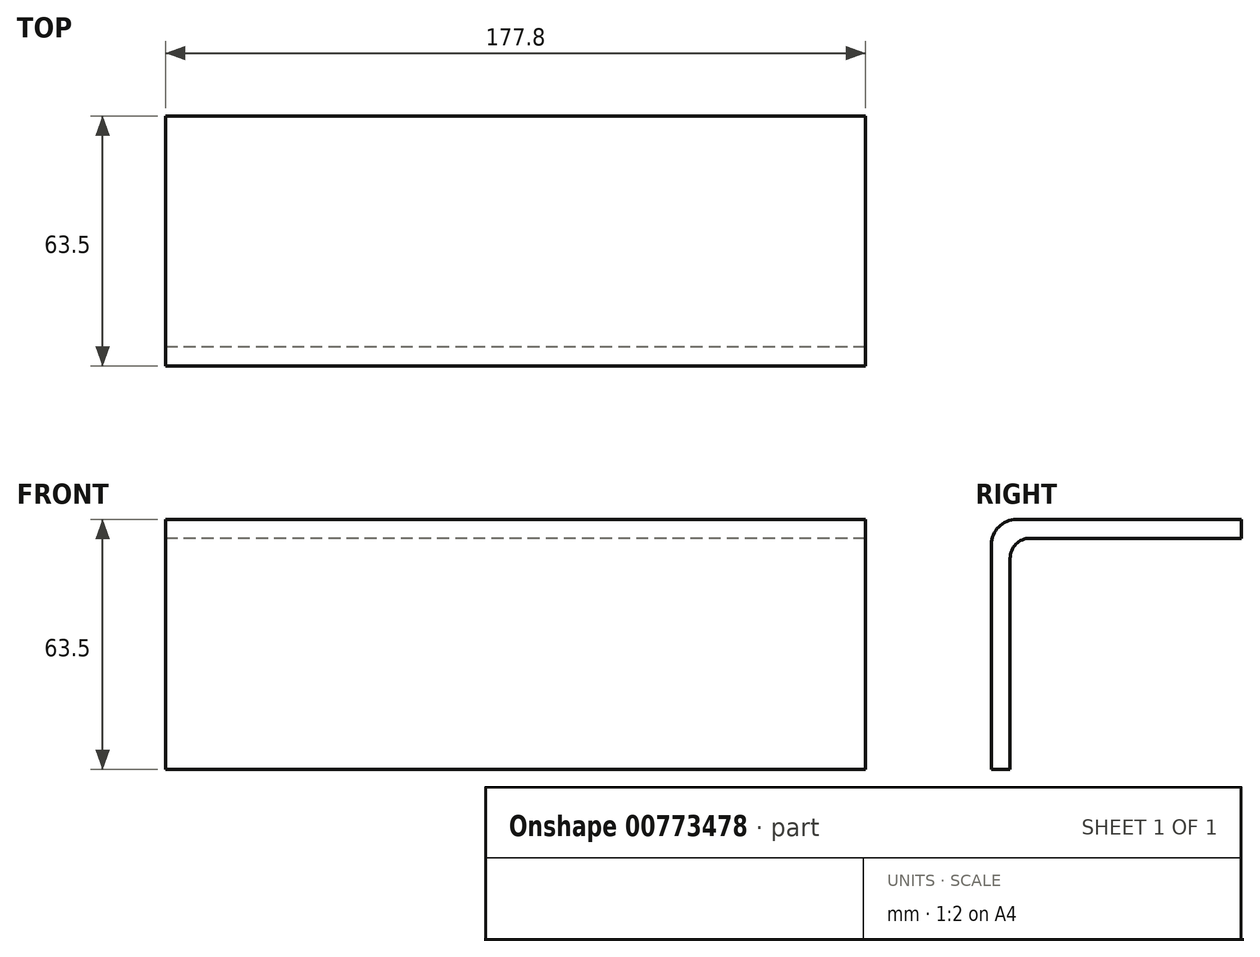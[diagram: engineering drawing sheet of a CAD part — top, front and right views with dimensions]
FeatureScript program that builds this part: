
annotation { "Feature Type Name" : "Feature", "Feature Type Description" : "" }
export const myFeature = defineFeature(function(context is Context, id is Id, definition is map)
    precondition{}
    {
        {
            var Q0;
            Q0=qCreatedBy(makeId("Right.planeOp"),FACE);
            var sketch = newSketch(context, id + "F0", { "sketchPlane" : qUnion([Q0])});
            skLineSegment(sketch, "E0", {"start": v(-28.12, -12.25) * mm, "end": v(-28.12, 44.9) * mm});
            skLineSegment(sketch, "E1", {"start": v(-21.77, 51.25) * mm, "end": v(35.38, 51.25) * mm});
            skPoint(sketch, "E2.visualSharp", {"position": v(-28.12, 51.25) * mm});
            skArc(sketch, "E2.filletArc", {"start": v(-21.77, 51.25) * mm, "mid": v(-26.26, 49.39) * mm, "end": v(-28.12, 44.9) * mm});
            skLineSegment(sketch, "E3", {"start": v(-28.12, -12.25) * mm, "end": v(-23.35, -12.25) * mm});
            skLineSegment(sketch, "E4", {"start": v(35.38, 51.25) * mm, "end": v(35.38, 46.48) * mm});
            skLineSegment(sketch, "E5", {"start": v(-23.35, -12.25) * mm, "end": v(-23.35, 41.4) * mm});
            skLineSegment(sketch, "E6", {"start": v(35.38, 46.48) * mm, "end": v(-18.27, 46.48) * mm});
            skPoint(sketch, "E7.newPointA", {"position": v(-23.35, 46.42) * mm});
            skPoint(sketch, "E7.newPointB", {"position": v(-23.29, 46.48) * mm});
            skArc(sketch, "E7.filletArc", {"start": v(-18.27, 46.48) * mm, "mid": v(-21.87, 45) * mm, "end": v(-23.35, 41.4) * mm});
            skSolve(sketch);
        }
        {
            var Q0;
            Q0=qSketchRegion(id+"F0",true);
            extrude(context, id + "F1", {"entities" : qUnion([Q0]), "depth" : 177.8 * mm, "offsetDistance" : 25.4 * mm});
        }
    });
